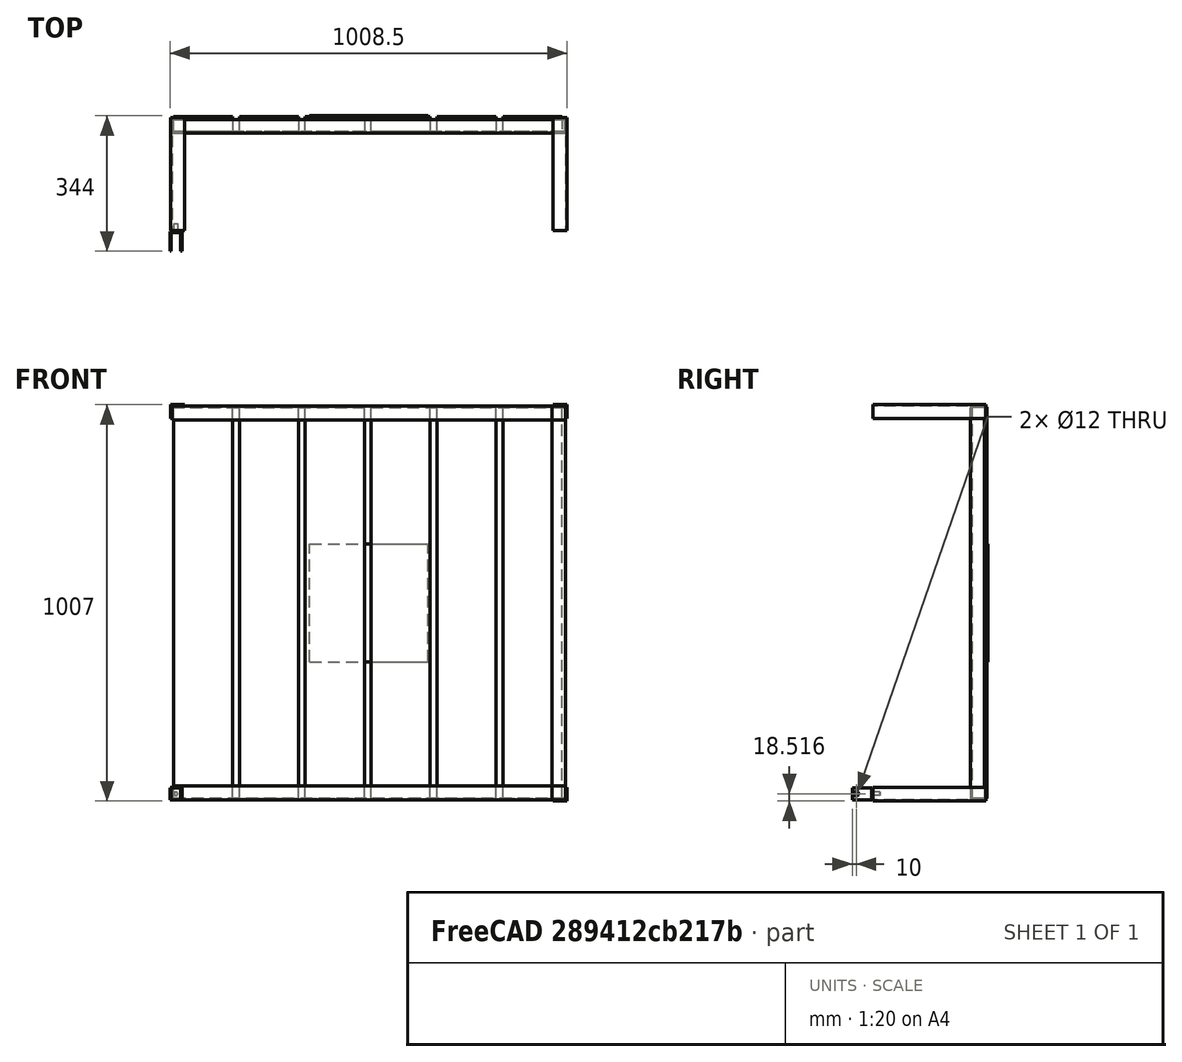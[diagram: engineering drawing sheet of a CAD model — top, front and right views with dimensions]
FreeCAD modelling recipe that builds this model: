
FCSTD DOCUMENT  (FreeCAD 0.18R16131 (Git))
Label: tableBasse
License: All rights reserved
LicenseURL: http://en.wikipedia.org/wiki/All_rights_reserved
objects: PartDesign::Body×10, Sketcher::SketchObject×6, PartDesign::FeatureBase×6, TechDraw::DrawViewDimension×6, PartDesign::Pad×5, TechDraw::DrawViewPart×5, App::DocumentObjectGroup×4, PartDesign::Plane×3, Part::FeaturePython×1, PartDesign::ShapeBinder×1, Part::Box×1, Spreadsheet::Sheet×1, PartDesign::Pocket×1, Part::Torus×1, TechDraw::DrawSVGTemplate×1, TechDraw::DrawPage×1
note: 41 computed .brp shape members not serialized (recipe doc carries the construction recipe); baked Part::Feature solids carry a one-line shape summary decoded from their .brp

FEATURE [Sketcher::SketchObject] Sketch
  MapMode = 5
  Support = -> [XY_Plane]
  sketch-geometry (6):
    g0: LineSegment StartX=35 StartY=0 StartZ=0 EndX=0 EndY=0 EndZ=0
    g1: LineSegment StartX=0 StartY=0 StartZ=0 EndX=0 EndY=35 EndZ=0
    g2: LineSegment StartX=0 StartY=35 StartZ=0 EndX=3.5 EndY=35 EndZ=0
    g3: LineSegment StartX=3.5 StartY=35 StartZ=0 EndX=3.5 EndY=3.5 EndZ=0
    g4: LineSegment StartX=3.5 StartY=3.5 StartZ=0 EndX=35 EndY=3.5 EndZ=0
    g5: LineSegment StartX=35 StartY=3.5 StartZ=0 EndX=35 EndY=0 EndZ=0
  constraints (17):
    c: PointOnObject(g0,g-1)
    c: Coincident(g0,g1)
    c: Vertical(g1)
    c: Coincident(g1,g2)
    c: Coincident(g2,g3)
    c: Vertical(g3)
    c: Coincident(g3,g4)
    c: Horizontal(g4)
    c: Coincident(g4,g5)
    c: Coincident(g5,g0)
    c: Vertical(g5)
    c: DistanceX(g0,g0) = 35
    c: DistanceY(g1,g1) = 35
    c: Horizontal(g2)
    c: DistanceY(g5,g5) = 3.5
    c: DistanceX(g2,g2) = 3.5
    c: Coincident(g0,g-1)
FEATURE [PartDesign::Pad] Pad  label="c1"
  Length = 1000
  Length2 = 100
  Profile = -> Sketch
  Type = 0
FEATURE [PartDesign::Body] Body  label="Cote1"
  Group = -> [Sketch,Pad]
  Origin = -> Origin
  Tip = -> Pad
FEATURE [PartDesign::FeatureBase] Clone  label="c2"
  BaseFeature = -> Pad
  Placement = pos=(0,0,1000) rot=(0,1,0;1.5708rad)
FEATURE [PartDesign::Body] Body001  label="Cote2"
  BaseFeature = -> Pad
  Group = -> [Clone]
  Origin = -> Origin001
  Tip = -> Clone
FEATURE [PartDesign::FeatureBase] Clone001  label="c3"
  BaseFeature = -> Body
  Placement = pos=(1000,0,0) rot=(0,-1,0;1.5708rad)
FEATURE [PartDesign::Body] Body002  label="Cote3"
  BaseFeature = -> Body
  Group = -> [Clone001]
  Origin = -> Origin002
  Tip = -> Clone001
FEATURE [PartDesign::FeatureBase] Clone002  label="c4"
  BaseFeature = -> Body
  Placement = pos=(1000,0,1000) rot=(0,1,0;3.14159rad)
FEATURE [PartDesign::Body] Body003  label="Cote4"
  BaseFeature = -> Body
  Group = -> [Clone002]
  Origin = -> Origin003
  Tip = -> Clone002
FEATURE [App::DocumentObjectGroup] Group  label="Support"
  Group = -> [Body,Body001,Body002,Body003]
FEATURE [Sketcher::SketchObject] Sketch002
  AttachmentOffset = pos=(-3.5,-3.5,-40) rot=(0,0,1;0rad)
  MapMode = 5
  Placement = pos=(-3.5,40,-3.5) rot=(1,0,0;1.5708rad)
  Support = -> [XZ_Plane004]
  sketch-geometry (6):
    g0: LineSegment StartX=3.5 StartY=3.5 StartZ=0 EndX=3.5 EndY=35 EndZ=0
    g1: LineSegment StartX=3.5 StartY=35 StartZ=0 EndX=0 EndY=35 EndZ=0
    g2: LineSegment StartX=0 StartY=35 StartZ=0 EndX=0 EndY=0 EndZ=0
    g3: LineSegment StartX=0 StartY=0 StartZ=0 EndX=35 EndY=0 EndZ=0
    g4: LineSegment StartX=35 StartY=0 StartZ=0 EndX=35 EndY=3.5 EndZ=0
    g5: LineSegment StartX=35 StartY=3.5 StartZ=0 EndX=3.5 EndY=3.5 EndZ=0
  constraints (17):
    c: Vertical(g0)
    c: Coincident(g0,g1)
    c: Coincident(g1,g2)
    c: Vertical(g2)
    c: Coincident(g2,g3)
    c: Horizontal(g3)
    c: Coincident(g3,g4)
    c: Vertical(g4)
    c: Coincident(g4,g5)
    c: Coincident(g5,g0)
    c: Horizontal(g5)
    c: DistanceX(g1,g1) = 3.5
    c: Coincident(g-1,g2)
    c: DistanceY(g4,g4) = 3.5
    c: DistanceX(g3,g3) = 35
    c: DistanceY(g2,g2) = 35
    c: Horizontal(g1)
FEATURE [PartDesign::Pad] Pad001
  Length = 288
  Length2 = 100
  Placement = pos=(0,0,0) rot=(1,0,0;1.5708rad)
  Profile = -> Sketch002
  Type = 0
FEATURE [PartDesign::Body] Body004
  Group = -> [Sketch002,Pad001]
  Origin = -> Origin004
  Tip = -> Pad001
FEATURE [PartDesign::FeatureBase] Clone003
  BaseFeature = -> Pad001
  Placement = pos=(0,0,1000) rot=(0.57735,0.57735,-0.57735;2.0944rad)
FEATURE [PartDesign::Body] Body005
  BaseFeature = -> Pad001
  Group = -> [Clone003]
  Origin = -> Origin005
  Tip = -> Clone003
FEATURE [PartDesign::FeatureBase] Clone004
  BaseFeature = -> Pad001
  Placement = pos=(0,0,2e-15) rot=(1,0,0;1.5708rad)
FEATURE [PartDesign::Body] Body006
  BaseFeature = -> Pad001
  Group = -> [Clone004]
  Origin = -> Origin006
  Placement = pos=(1000,0,0) rot=(0,-1,0;1.5708rad)
  Tip = -> Clone004
FEATURE [PartDesign::FeatureBase] Clone005
  BaseFeature = -> Body004
  Placement = pos=(1000,0,1000) rot=(0,1,0;3.14159rad)
FEATURE [PartDesign::Body] Body007
  BaseFeature = -> Body004
  Group = -> [Clone005]
  Origin = -> Origin007
  Tip = -> Clone005
FEATURE [App::DocumentObjectGroup] Group001  label="Pieds"
  Group = -> [Body004,Body005,Body006,Body007]
FEATURE [Sketcher::SketchObject] Sketch003
  AttachmentOffset = pos=(3.5,3.5,3.5) rot=(0,0,1;0rad)
  MapMode = 5
  Placement = pos=(3.5,3.5,3.5) rot=(0,0,1;0rad)
  Support = -> [XY_Plane008]
  sketch-geometry (4):
    g0: LineSegment StartX=0 StartY=38 StartZ=0 EndX=150 EndY=38 EndZ=0
    g1: LineSegment StartX=150 StartY=38 StartZ=0 EndX=150 EndY=0 EndZ=0
    g2: LineSegment StartX=150 StartY=0 StartZ=0 EndX=0 EndY=0 EndZ=0
    g3: LineSegment StartX=0 StartY=0 StartZ=0 EndX=0 EndY=38 EndZ=0
  constraints (11):
    c: Coincident(g0,g1)
    c: Coincident(g1,g2)
    c: Coincident(g2,g3)
    c: Coincident(g3,g0)
    c: Horizontal(g0)
    c: Horizontal(g2)
    c: Vertical(g1)
    c: Vertical(g3)
    c: DistanceY(g1,g1) = 38
    c: DistanceX(g0,g0) = 150
    c: Coincident(g-1,g2)
FEATURE [PartDesign::Pad] Pad002
  Length = 994
  Length2 = 100
  Profile = -> Sketch003
  Type = 0
FEATURE [Part::FeaturePython] Array  # Draft array (typed FeaturePython)
  Angle = 360
  ArrayType = 0
  Axis = (0,0,1)
  Base = -> Pad002
  Center = (0,0,0)
  Fuse = false
  IntervalAxis = (0,0,0)
  IntervalX = (167.5,0,0)
  IntervalY = (0,0,0)
  IntervalZ = (0,0,0)
  NumberPolar = 1
  NumberX = 6
  NumberY = 2
  NumberZ = 1
FEATURE [PartDesign::ShapeBinder] ReferenceArray
  Placement = pos=(335,0,0) rot=(0,0,1;0rad)
  Support = -> [Array]
  TraceSupport = false
FEATURE [PartDesign::Plane] DatumPlane
  Length = 462.913
  MapMode = 5
  Placement = pos=(335,41.5,0) rot=(0,0.707107,0.707107;3.14159rad)
  ResizeMode = 0
  Support = -> [ReferenceArray]
  Width = 1125.41
FEATURE [PartDesign::Body] Body008
  Group = -> [Sketch003,Pad002,DatumPlane,ReferenceArray]
  Origin = -> Origin008
  Tip = -> Pad002
FEATURE [Part::Box] Box  label="Cube"
  AttacherType = Attacher::AttachEngine3D
  Height = 300
  Length = 300
  Placement = pos=(350,41,350) rot=(0,0,1;0rad)
  Width = 3
FEATURE [App::DocumentObjectGroup] Group002  label="Plan"
  Group = -> [Body008,Array,Box]
FEATURE [Spreadsheet::Sheet] Spreadsheet
  cells = A2=Corniere; B2=35x35x3,5 2.5ML; C2=https://www.bricoman.fr/corniere-acier-lamine-a-chaud-35x35-l250cm.html; A3=Bois; B3=38x150 4ML; C3=https://www.bricoman.fr/solive-38x150-mm-4ml.html; A4=Roulette; B4=d50 62; C4=https://www.leroymerlin.fr/v3/p/produits/roulette-pivotante-a-tige-filetee-diam-50-mm-e21406; A6=dimension HT; B6=100x100x35
FEATURE [Sketcher::SketchObject] Sketch004
  MapMode = 5
  Support = -> [XY_Plane009]
  sketch-geometry (8):
    g0: LineSegment StartX=-12 StartY=0 StartZ=0 EndX=-15 EndY=0 EndZ=0
    g1: LineSegment StartX=-15 StartY=0 StartZ=0 EndX=-15 EndY=50 EndZ=0
    g2: LineSegment StartX=-15 StartY=50 StartZ=0 EndX=15 EndY=50 EndZ=0
    g3: LineSegment StartX=15 StartY=50 StartZ=0 EndX=15 EndY=0 EndZ=0
    g4: LineSegment StartX=15 StartY=0 StartZ=0 EndX=12 EndY=0 EndZ=0
    g5: LineSegment StartX=12 StartY=0 StartZ=0 EndX=12 EndY=47 EndZ=0
    g6: LineSegment StartX=12 StartY=47 StartZ=0 EndX=-12 EndY=47 EndZ=0
    g7: LineSegment StartX=-12 StartY=47 StartZ=0 EndX=-12 EndY=0 EndZ=0
  constraints (23):
    c: Horizontal(g0)
    c: Coincident(g0,g1)
    c: Vertical(g1)
    c: Coincident(g1,g2)
    c: Horizontal(g2)
    c: Coincident(g2,g3)
    c: Vertical(g3)
    c: Coincident(g3,g4)
    c: Horizontal(g4)
    c: Coincident(g4,g5)
    c: Vertical(g5)
    c: Coincident(g5,g6)
    c: Horizontal(g6)
    c: Coincident(g6,g7)
    c: Coincident(g7,g0)
    c: Vertical(g7)
    c: DistanceX(g0,g0) = 3
    c: DistanceX(g4,g4) = 3
    c: DistanceY(g5,g2) = 3
    c: DistanceY(g3,g3) = 50
    c: Equal(g3,g1)
    c: DistanceX(g2,g2) = 30
    c: Symmetric(g0,g4,g-1)
FEATURE [PartDesign::Pad] Pad003
  Length = 30
  Length2 = 100
  Profile = -> Sketch004
  Type = 0
FEATURE [PartDesign::Plane] DatumPlane001
  Length = 91.3137
  MapMode = 5
  Placement = pos=(15,0,0) rot=(0.57735,0.57735,0.57735;2.0944rad)
  ResizeMode = 0
  Support = -> [Pad003]
  Width = 51.3137
FEATURE [Sketcher::SketchObject] Sketch005
  ExternalGeometry = -> [Pad003,Sketch004]
  MapMode = 5
  Placement = pos=(15,0,0) rot=(0.57735,0.57735,0.57735;2.0944rad)
  Support = -> [DatumPlane001]
  sketch-geometry (1):
    g0: Circle CenterX=10 CenterY=15.016 CenterZ=0 NormalX=0 NormalY=0 NormalZ=1 AngleXU=0 Radius=6
  constraints (2):
    c: Radius(g0) = 6
    c: DistanceX(g-5,g0) = 10
FEATURE [PartDesign::Pocket] Pocket
  BaseFeature = -> Pad003
  Length = 5
  Length2 = 100
  Profile = -> Sketch005
  Type = 1
FEATURE [PartDesign::Plane] DatumPlane002
  Length = 36.9282
  MapMode = 5
  Placement = pos=(0,50,0) rot=(0,0.707107,0.707107;3.14159rad)
  ResizeMode = 0
  Support = -> [Pocket]
  Width = 46.9282
FEATURE [Sketcher::SketchObject] Sketch006
  ExternalGeometry = -> [Pocket,Sketch004]
  MapMode = 5
  Placement = pos=(0,50,0) rot=(0,0.707107,0.707107;3.14159rad)
  Support = -> [DatumPlane002]
  sketch-geometry (3):
    g0: LineSegment [constr] StartX=-15 StartY=30 StartZ=0 EndX=15 EndY=0 EndZ=0
    g1: LineSegment [constr] StartX=15 StartY=30 StartZ=0 EndX=-15 EndY=0 EndZ=0
    g2: Circle CenterX=9e-16 CenterY=15 CenterZ=0 NormalX=0 NormalY=0 NormalZ=1 AngleXU=0 Radius=4.23215
  constraints (6):
    c: Coincident(g0,g-3)
    c: Coincident(g0,g-4)
    c: Coincident(g1,g-3)
    c: Coincident(g1,g-4)
    c: PointOnObject(g2,g0)
    c: PointOnObject(g2,g1)
FEATURE [PartDesign::Pad] Pad004
  BaseFeature = -> Pocket
  Length = 20
  Length2 = 100
  Profile = -> Sketch006
  Type = 0
FEATURE [PartDesign::Body] Body009  label="r1"
  Group = -> [Sketch004,Pad003,DatumPlane001,Sketch005,Pocket,DatumPlane002,Sketch006,Pad004]
  Origin = -> Origin009
  Placement = pos=(10,-300,0) rot=(0,0,1;0rad)
  Tip = -> Pad004
FEATURE [App::DocumentObjectGroup] Group003  label="Roue"
  Group = -> [Body009]
FEATURE [Part::Torus] Torus  label="Tore"
  Angle1 = 9
  Angle2 = 0
  Angle3 = 360
  AttacherType = Attacher::AttachEngine3D
  Placement = pos=(10,-290,15) rot=(0,1,0;1.5708rad)
  Radius1 = 15
  Radius2 = 5
FEATURE [TechDraw::DrawSVGTemplate] Template
  EditableTexts = Designed_by_Name=Designed by Name; Drawing_number=Drawing number; FC-Date=Date; FC-SC=Scale; FC-SH=Sheet; FC-Title=Title; Subtitle=Subtitle; Weight=Weight
  Height = 210
  Orientation = 1
  Width = 297
FEATURE [TechDraw::DrawViewPart] View
  CoarseView = false
  Direction = (0,0,1)
  Focus = 100
  HardHidden = false
  IsoCount = 0
  IsoHidden = false
  IsoVisible = false
  LockPosition = false
  Perspective = false
  Rotation = 0
  Scale = 0.1
  ScaleType = 0
  SeamHidden = false
  SeamVisible = false
  SmoothHidden = false
  SmoothVisible = false
  Source = -> [Group,Group002,Group001]
  X = 86.7353
  Y = 165.258
FEATURE [TechDraw::DrawViewPart] View002
  CoarseView = false
  Direction = (0,0,1)
  Focus = 100
  HardHidden = false
  IsoCount = 0
  IsoHidden = false
  IsoVisible = false
  LockPosition = false
  Perspective = false
  Rotation = 0
  Scale = 0.2
  ScaleType = 0
  SeamHidden = false
  SeamVisible = false
  SmoothHidden = false
  SmoothVisible = false
  Source = -> [Body]
  X = 177.358
  Y = 176.278
FEATURE [TechDraw::DrawViewDimension] Dimension002
  Arbitrary = false
  FormatSpec = %.2f
  LockPosition = false
  MeasureType = 1
  OverTolerance = 0
  References2D = -> [View002]
  Rotation = 0
  ScaleType = 0
  Type = 1
  UnderTolerance = 0
  X = -11.5113
  Y = -15.8429
FEATURE [TechDraw::DrawViewDimension] Dimension003
  Arbitrary = false
  FormatSpec = %.2f
  LockPosition = false
  MeasureType = 1
  OverTolerance = 0
  References2D = -> [View002]
  Rotation = 0
  ScaleType = 0
  Type = 2
  UnderTolerance = 0
  X = -20.2002
  Y = 12.1456
FEATURE [TechDraw::DrawViewDimension] Dimension004
  Arbitrary = false
  FormatSpec = %.2f
  LockPosition = false
  MeasureType = 1
  OverTolerance = 0
  References2D = -> [View002]
  Rotation = 0
  ScaleType = 0
  Type = 1
  UnderTolerance = 0
  X = 8.82041
  Y = 13.4267
FEATURE [TechDraw::DrawViewPart] View004
  CoarseView = false
  Direction = (0.583,0.435,0.686)
  Focus = 100
  HardHidden = false
  IsoCount = 0
  IsoHidden = false
  IsoVisible = false
  LockPosition = false
  Perspective = false
  Rotation = 225
  Scale = 0.05
  ScaleType = 0
  SeamHidden = false
  SeamVisible = false
  SmoothHidden = false
  SmoothVisible = false
  Source = -> [Group,Group002,Group001]
  X = 242.026
  Y = 167.978
FEATURE [TechDraw::DrawViewPart] View005
  CoarseView = false
  Direction = (0,1,0)
  Focus = 100
  HardHidden = false
  IsoCount = 0
  IsoHidden = false
  IsoVisible = false
  LockPosition = false
  Perspective = false
  Rotation = 0
  Scale = 0.1
  ScaleType = 0
  SeamHidden = false
  SeamVisible = false
  SmoothHidden = false
  SmoothVisible = false
  Source = -> [Group,Group002,Group001]
  X = 84.0406
  Y = 82.528
FEATURE [TechDraw::DrawViewDimension] Dimension007
  Arbitrary = false
  FormatSpec = %.2f
  LockPosition = false
  MeasureType = 1
  OverTolerance = 0
  References2D = -> [View005]
  Rotation = 0
  ScaleType = 0
  Type = 1
  UnderTolerance = 0
  X = 1.04578
  Y = -55.3958
FEATURE [TechDraw::DrawViewDimension] Dimension008
  Arbitrary = false
  FormatSpec = %.2f
  LockPosition = false
  MeasureType = 1
  OverTolerance = 0
  References2D = -> [View005]
  Rotation = 0
  ScaleType = 0
  Type = 2
  UnderTolerance = 0
  X = -65.7517
  Y = 0.290597
FEATURE [TechDraw::DrawViewPart] View006
  CoarseView = false
  Direction = (-0.65,0.389,-0.653)
  Focus = 100
  HardHidden = false
  IsoCount = 0
  IsoHidden = false
  IsoVisible = false
  LockPosition = false
  Perspective = false
  Rotation = 45
  Scale = 0.1
  ScaleType = 0
  SeamHidden = false
  SeamVisible = false
  SmoothHidden = false
  SmoothVisible = false
  Source = -> [Pad002]
  X = 183.253
  Y = 100.583
FEATURE [TechDraw::DrawViewDimension] Dimension009
  Arbitrary = false
  FormatSpec = %.2f
  LockPosition = false
  MeasureType = 1
  OverTolerance = 0
  References2D = -> [View]
  Rotation = 0
  ScaleType = 0
  Type = 2
  UnderTolerance = 0
  X = -68.1726
  Y = 0.130048
FEATURE [TechDraw::DrawPage] Page
  KeepUpdated = true
  ProjectionType = 0
  Template = -> Template
  Views = -> [View,View002,Dimension002,Dimension003,Dimension004,View004,View005,Dimension007,Dimension008,View006,Dimension009]
